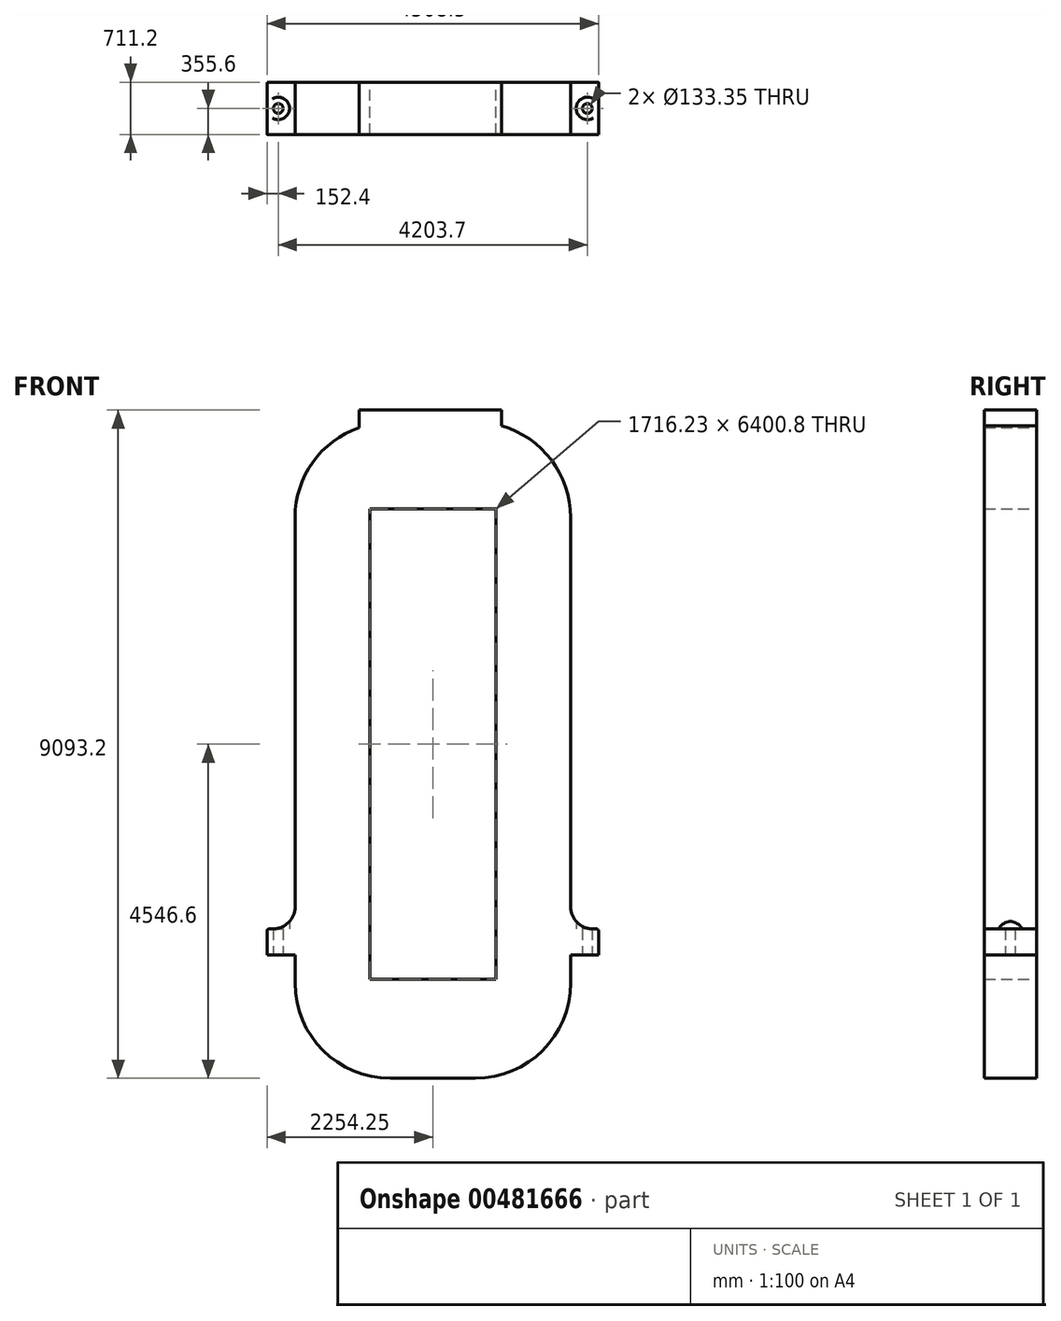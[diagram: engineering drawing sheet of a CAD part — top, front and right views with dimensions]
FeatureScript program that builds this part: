
annotation { "Feature Type Name" : "Feature", "Feature Type Description" : "" }
export const myFeature = defineFeature(function(context is Context, id is Id, definition is map)
    precondition{}
    {
        {
            var Q0;
            Q0=qCreatedBy(makeId("Front.planeOp"),FACE);
            var sketch = newSketch(context, id + "F0", { "sketchPlane" : qUnion([Q0])});
            skLineSegment(sketch, "E0.bottom", {"start": v(-1003.3, 4546.6) * mm, "end": v(931.93, 4546.6) * mm});
            skLineSegment(sketch, "E0.top", {"start": v(-577.85, -4546.6) * mm, "end": v(577.85, -4546.6) * mm});
            skLineSegment(sketch, "E0.left", {"start": v(-2254.25, -2514.6) * mm, "end": v(-2254.25, -2870.2) * mm});
            skPoint(sketch, "E0.middle", {"position": v(0, 0) * mm});
            skLineSegment(sketch, "E1.bottom", {"start": v(-858.11, 3200.4) * mm, "end": v(858.11, 3200.4) * mm});
            skLineSegment(sketch, "E1.top", {"start": v(-858.11, -3200.4) * mm, "end": v(858.11, -3200.4) * mm});
            skLineSegment(sketch, "E1.left", {"start": v(-858.11, 3200.4) * mm, "end": v(-858.11, -3200.4) * mm});
            skLineSegment(sketch, "E1.right", {"start": v(858.11, 3200.4) * mm, "end": v(858.11, -3200.4) * mm});
            skLineSegment(sketch, "E2", {"start": v(0, 5961.94) * mm, "end": v(0, -6325.17) * mm, "construction": true});
            skLineSegment(sketch, "E3.0", {"start": v(-1873.25, 3086.1) * mm, "end": v(-1873.25, -2209.8) * mm});
            skPoint(sketch, "E4.newPointB", {"position": v(-2254.25, -4546.6) * mm});
            skArc(sketch, "E4.filletArc", {"start": v(-1873.25, -3251.2) * mm, "mid": v(-1493.84, -4167.19) * mm, "end": v(-577.85, -4546.6) * mm});
            skArc(sketch, "E5.MirrorCS", {"start": v(1873.25, -3251.2) * mm, "mid": v(1493.84, -4167.19) * mm, "end": v(577.85, -4546.6) * mm});
            skLineSegment(sketch, "E6", {"start": v(-773.14, -3200.4) * mm, "end": v(-858.11, -3200.4) * mm, "construction": true});
            skLineSegment(sketch, "E7.0", {"start": v(-2178.05, -2514.6) * mm, "end": v(-2254.25, -2514.6) * mm});
            skArc(sketch, "E8.filletArc", {"start": v(-2178.05, -2514.6) * mm, "mid": v(-1962.52, -2425.33) * mm, "end": v(-1873.25, -2209.8) * mm});
            skLineSegment(sketch, "E9", {"start": v(-1873.25, -2870.2) * mm, "end": v(-1873.25, -3251.2) * mm});
            skLineSegment(sketch, "E10.trimOffspring", {"start": v(-1873.25, -2870.2) * mm, "end": v(-2254.25, -2870.2) * mm});
            skLineSegment(sketch, "E11.MirrorCS", {"start": v(2178.05, -2514.6) * mm, "end": v(2254.25, -2514.6) * mm});
            skLineSegment(sketch, "E12.MirrorCS", {"start": v(2254.25, -2514.6) * mm, "end": v(2254.25, -2870.2) * mm});
            skLineSegment(sketch, "E13.MirrorCS", {"start": v(1873.25, -2870.2) * mm, "end": v(1873.25, -3251.2) * mm});
            skArc(sketch, "E14.MirrorCS", {"start": v(2178.05, -2514.6) * mm, "mid": v(1962.52, -2425.33) * mm, "end": v(1873.25, -2209.8) * mm});
            skLineSegment(sketch, "E15.MirrorCS", {"start": v(1873.25, -2870.2) * mm, "end": v(2254.25, -2870.2) * mm});
            skLineSegment(sketch, "E16.MirrorCS", {"start": v(1873.25, 3086.1) * mm, "end": v(1873.25, -2209.8) * mm});
            skPoint(sketch, "E17.newPointB", {"position": v(-1873.25, 5961.94) * mm});
            skArc(sketch, "E17.filletArc", {"start": v(-1003.3, 4309.64) * mm, "mid": v(-1633.6, 3836.74) * mm, "end": v(-1873.25, 3086.1) * mm});
            skPoint(sketch, "E18.newPointB", {"position": v(1873.25, 5961.94) * mm});
            skArc(sketch, "E18.filletArc", {"start": v(1873.25, 3086.1) * mm, "mid": v(1611.47, 3866.93) * mm, "end": v(931.93, 4332.17) * mm});
            skLineSegment(sketch, "E19.0", {"start": v(-1003.3, 4546.6) * mm, "end": v(-1003.3, 4309.64) * mm});
            skLineSegment(sketch, "E20.0", {"start": v(931.93, 4546.6) * mm, "end": v(931.93, 4332.17) * mm});
            skLineSegment(sketch, "E21.trimOffspring", {"start": v(-1003.3, -4474.74) * mm, "end": v(-1003.3, -6325.17) * mm});
            skPoint(sketch, "E22.orphan", {"position": v(2254.25, 4546.6) * mm});
            skLineSegment(sketch, "E23.trimOffspring", {"start": v(931.93, -4497.27) * mm, "end": v(931.93, -6325.17) * mm});
            skPoint(sketch, "E24.orphan", {"position": v(-2254.25, 4546.6) * mm});
            skPoint(sketch, "E25.orphan", {"position": v(2254.25, -4546.6) * mm});
            skSolve(sketch);
        }
        {
            var Q0;
            Q0 = qSketchRegion(id + "F0", true);
            extrude(context, id + "F1", {"entities" : qUnion([Q0]), "endBound" : BoundingType.SYMMETRIC, "depth" : 711.2 * mm});
        }
        {
            var Q0;
            Q0=makeQuery(id+"F1.opExtrude","SWEPT_EDGE",EDGE,{"disambiguationData":[OSD([sQuery(id+"F0.wireOp",EDGE,"E11.MirrorCS"),sQuery(id+"F0.wireOp",EDGE,"E12.MirrorCS")])]});
            var Q1;
            Q1=makeQuery(id+"F1.opExtrude","SWEPT_EDGE",EDGE,{"disambiguationData":[OSD([sQuery(id+"F0.wireOp",EDGE,"E0.left"),sQuery(id+"F0.wireOp",EDGE,"E7.0")])]});
            fillet(context, id + "F2", {"entities" : qUnion([Q0, Q1]), "radius" : 25.4 * mm, "tangentPropagation" : true, "allowEdgeOverflow" : false});
        }
        {
            var Q0;
            Q0=makeQuery(id+"F1.opExtrude","SWEPT_FACE",FACE,{"disambiguationData":[OSD([sQuery(id+"F0.wireOp",EDGE,"E15.MirrorCS")])]});
            var sketch = newSketch(context, id + "F3", { "sketchPlane" : qUnion([Q0])});
            skLineSegment(sketch, "E26", {"start": v(-2832.44, 0) * mm, "end": v(2786.75, 0) * mm, "construction": true});
            skLineSegment(sketch, "E27", {"start": v(0, 1318.64) * mm, "end": v(0, -1093.87) * mm, "construction": true});
            skLineSegment(sketch, "E28.0", {"start": v(-2101.85, 1318.64) * mm, "end": v(-2101.85, -1093.87) * mm, "construction": true});
            skPoint(sketch, "E29", {"position": v(-2101.85, 0) * mm});
            skPoint(sketch, "E30.MirrorP", {"position": v(2101.85, 0) * mm});
            skSolve(sketch);
        }
        {
            var Q0;
            Q0=sQuery(id+"F3.wireOp",VERTEX,"E29");
            var Q1;
            Q1=sQuery(id+"F3.wireOp",VERTEX,"E30.MirrorP");
            var Q2;
            Q2=makeQuery(id+"F1.opExtrude","SWEPT_BODY",BODY,{"disambiguationData":[OSD([sQuery(id+"F0.wireOp",EDGE,"E0.bottom"),sQuery(id+"F0.wireOp",EDGE,"E0.top"),sQuery(id+"F0.wireOp",EDGE,"E0.left"),sQuery(id+"F0.wireOp",EDGE,"E1.bottom"),sQuery(id+"F0.wireOp",EDGE,"E1.top"),sQuery(id+"F0.wireOp",EDGE,"E1.left"),sQuery(id+"F0.wireOp",EDGE,"E1.right"),sQuery(id+"F0.wireOp",EDGE,"E3.0"),sQuery(id+"F0.wireOp",EDGE,"E4.filletArc"),sQuery(id+"F0.wireOp",EDGE,"E5.MirrorCS"),sQuery(id+"F0.wireOp",EDGE,"E7.0"),sQuery(id+"F0.wireOp",EDGE,"E8.filletArc"),sQuery(id+"F0.wireOp",EDGE,"E9"),sQuery(id+"F0.wireOp",EDGE,"E10.trimOffspring"),sQuery(id+"F0.wireOp",EDGE,"E11.MirrorCS"),sQuery(id+"F0.wireOp",EDGE,"E12.MirrorCS"),sQuery(id+"F0.wireOp",EDGE,"E13.MirrorCS"),sQuery(id+"F0.wireOp",EDGE,"E14.MirrorCS"),sQuery(id+"F0.wireOp",EDGE,"E15.MirrorCS"),sQuery(id+"F0.wireOp",EDGE,"E16.MirrorCS"),sQuery(id+"F0.wireOp",EDGE,"E17.filletArc"),sQuery(id+"F0.wireOp",EDGE,"E18.filletArc"),sQuery(id+"F0.wireOp",EDGE,"E19.0"),sQuery(id+"F0.wireOp",EDGE,"E20.0")])]});
            hole(context, id + "F4", {"style" : HoleStyle.SIMPLE, "endStyle" : HoleEndStyle.THROUGH, "holeDiameter" : 133.35 * mm, "isTappedThrough" : true, "tappedDepth" : 15.24 * mm, "tapClearance" : 3, "locations" : qUnion([Q0, Q1]), "scope" : qUnion([Q2])});
        }
        {
            var Q0;
            Q0=makeQuery(id+"F1.opExtrude","SWEPT_FACE",FACE,{"disambiguationData":[OSD([sQuery(id+"F0.wireOp",EDGE,"E11.MirrorCS")])]});
            var sketch = newSketch(context, id + "F5", { "sketchPlane" : qUnion([Q0])});
            skCircle(sketch, "E31.0", {"center": v(-2101.85, 0) * mm, "radius": 66.67 * mm, "construction": true});
            skCircle(sketch, "E32.0", {"center": v(2101.85, 0) * mm, "radius": 66.67 * mm, "construction": true});
            skCircle(sketch, "E33", {"center": v(-2101.85, 0) * mm, "radius": 152.4 * mm});
            skLineSegment(sketch, "E34", {"start": v(0, 799.27) * mm, "end": v(0, -714.14) * mm, "construction": true});
            skCircle(sketch, "E35.MirrorC", {"center": v(2101.85, 0) * mm, "radius": 152.4 * mm});
            skSolve(sketch);
        }
        {
            var Q0;
            Q0 = qSketchRegion(id + "F5", true);
            extrude(context, id + "F6", {"entities" : qUnion([Q0]), "operationType" : NewBodyOperationType.REMOVE, "endBound" : BoundingType.THROUGH_ALL, "depth" : 25.4 * mm});
        }
    });
